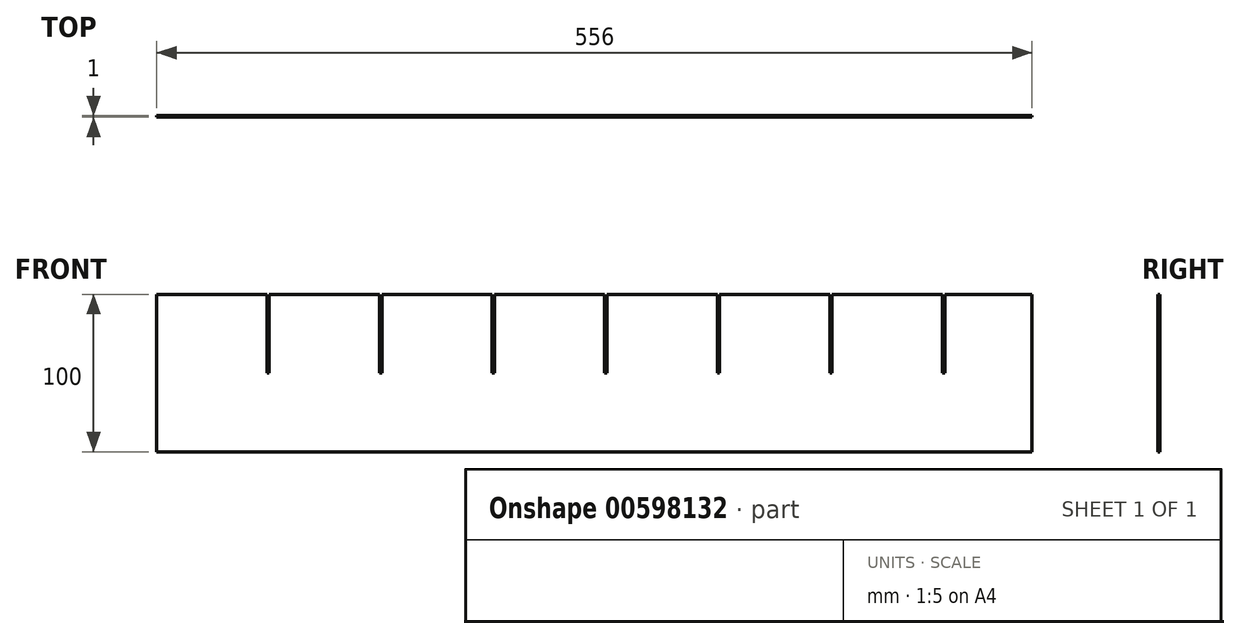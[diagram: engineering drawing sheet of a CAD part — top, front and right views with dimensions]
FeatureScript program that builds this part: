
annotation { "Feature Type Name" : "Feature", "Feature Type Description" : "" }
export const myFeature = defineFeature(function(context is Context, id is Id, definition is map)
    precondition{}
    {
        {
            var Q0;
            Q0=qCreatedBy(makeId("Front.planeOp"),FACE);
            var sketch = newSketch(context, id + "F0", { "sketchPlane" : qUnion([Q0])});
            skLineSegment(sketch, "E0", {"start": v(-106.93, -63.3) * mm, "end": v(-106.93, 36.7) * mm});
            skLineSegment(sketch, "E1", {"start": v(-106.93, 36.7) * mm, "end": v(-36.93, 36.7) * mm});
            skLineSegment(sketch, "E2", {"start": v(-36.93, 36.7) * mm, "end": v(-36.93, -13.3) * mm});
            skLineSegment(sketch, "E3", {"start": v(-36.93, -13.3) * mm, "end": v(-35.43, -13.3) * mm});
            skLineSegment(sketch, "E4", {"start": v(-35.43, -13.3) * mm, "end": v(-35.43, 36.7) * mm});
            skLineSegment(sketch, "E5", {"start": v(-35.43, 36.7) * mm, "end": v(34.57, 36.7) * mm});
            skLineSegment(sketch, "E6", {"start": v(34.57, 36.7) * mm, "end": v(34.57, -13.3) * mm});
            skLineSegment(sketch, "E7", {"start": v(34.57, -13.3) * mm, "end": v(36.07, -13.3) * mm});
            skLineSegment(sketch, "E8", {"start": v(36.07, -13.3) * mm, "end": v(36.07, 36.7) * mm});
            skLineSegment(sketch, "E9", {"start": v(36.07, 36.7) * mm, "end": v(106.07, 36.7) * mm});
            skLineSegment(sketch, "E10", {"start": v(106.07, 36.7) * mm, "end": v(106.07, -13.3) * mm});
            skLineSegment(sketch, "E11", {"start": v(106.07, -13.3) * mm, "end": v(107.57, -13.3) * mm});
            skLineSegment(sketch, "E12", {"start": v(107.57, -13.3) * mm, "end": v(107.57, 36.7) * mm});
            skLineSegment(sketch, "E13", {"start": v(107.57, 36.7) * mm, "end": v(177.57, 36.7) * mm});
            skLineSegment(sketch, "E14", {"start": v(177.57, 36.7) * mm, "end": v(177.57, -13.3) * mm});
            skLineSegment(sketch, "E15", {"start": v(177.57, -13.3) * mm, "end": v(179.07, -13.3) * mm});
            skLineSegment(sketch, "E16", {"start": v(179.07, -13.3) * mm, "end": v(179.07, 36.7) * mm});
            skLineSegment(sketch, "E17", {"start": v(179.07, 36.7) * mm, "end": v(249.07, 36.7) * mm});
            skLineSegment(sketch, "E18", {"start": v(249.07, 36.7) * mm, "end": v(249.07, -13.3) * mm});
            skLineSegment(sketch, "E19", {"start": v(249.07, -13.3) * mm, "end": v(250.57, -13.3) * mm});
            skLineSegment(sketch, "E20", {"start": v(250.57, -13.3) * mm, "end": v(250.57, 36.7) * mm});
            skLineSegment(sketch, "E21", {"start": v(250.57, 36.7) * mm, "end": v(320.57, 36.7) * mm});
            skLineSegment(sketch, "E22", {"start": v(320.57, 36.7) * mm, "end": v(320.57, -13.3) * mm});
            skLineSegment(sketch, "E23", {"start": v(320.57, -13.3) * mm, "end": v(322.07, -13.3) * mm});
            skLineSegment(sketch, "E24", {"start": v(322.07, -13.3) * mm, "end": v(322.07, 36.7) * mm});
            skLineSegment(sketch, "E25", {"start": v(322.07, 36.7) * mm, "end": v(392.07, 36.7) * mm});
            skLineSegment(sketch, "E26", {"start": v(392.07, 36.7) * mm, "end": v(392.07, -13.3) * mm});
            skLineSegment(sketch, "E27", {"start": v(392.07, -13.3) * mm, "end": v(393.57, -13.3) * mm});
            skLineSegment(sketch, "E28", {"start": v(393.57, -13.3) * mm, "end": v(393.57, 36.7) * mm});
            skLineSegment(sketch, "E29", {"start": v(393.57, 36.7) * mm, "end": v(449.07, 36.7) * mm});
            skLineSegment(sketch, "E30", {"start": v(449.07, 36.7) * mm, "end": v(449.07, -63.3) * mm});
            skLineSegment(sketch, "E31", {"start": v(449.07, -63.3) * mm, "end": v(-106.93, -63.3) * mm});
            skSolve(sketch);
        }
        {
            var Q0;
            Q0=makeQuery(id+"F0.imprint","IMPRINT",FACE,{"disambiguationData":[TD([[makeQuery(id+"F0.imprint","IMPRINT",EDGE,{"derivedFrom":sQuery(id+"F0.wireOp",EDGE,"E0")}),-1.0]])]});
            extrude(context, id + "F1", {"entities" : qUnion([Q0]), "depth" : 1 * mm, "offsetDistance" : 25 * mm});
        }
    });
